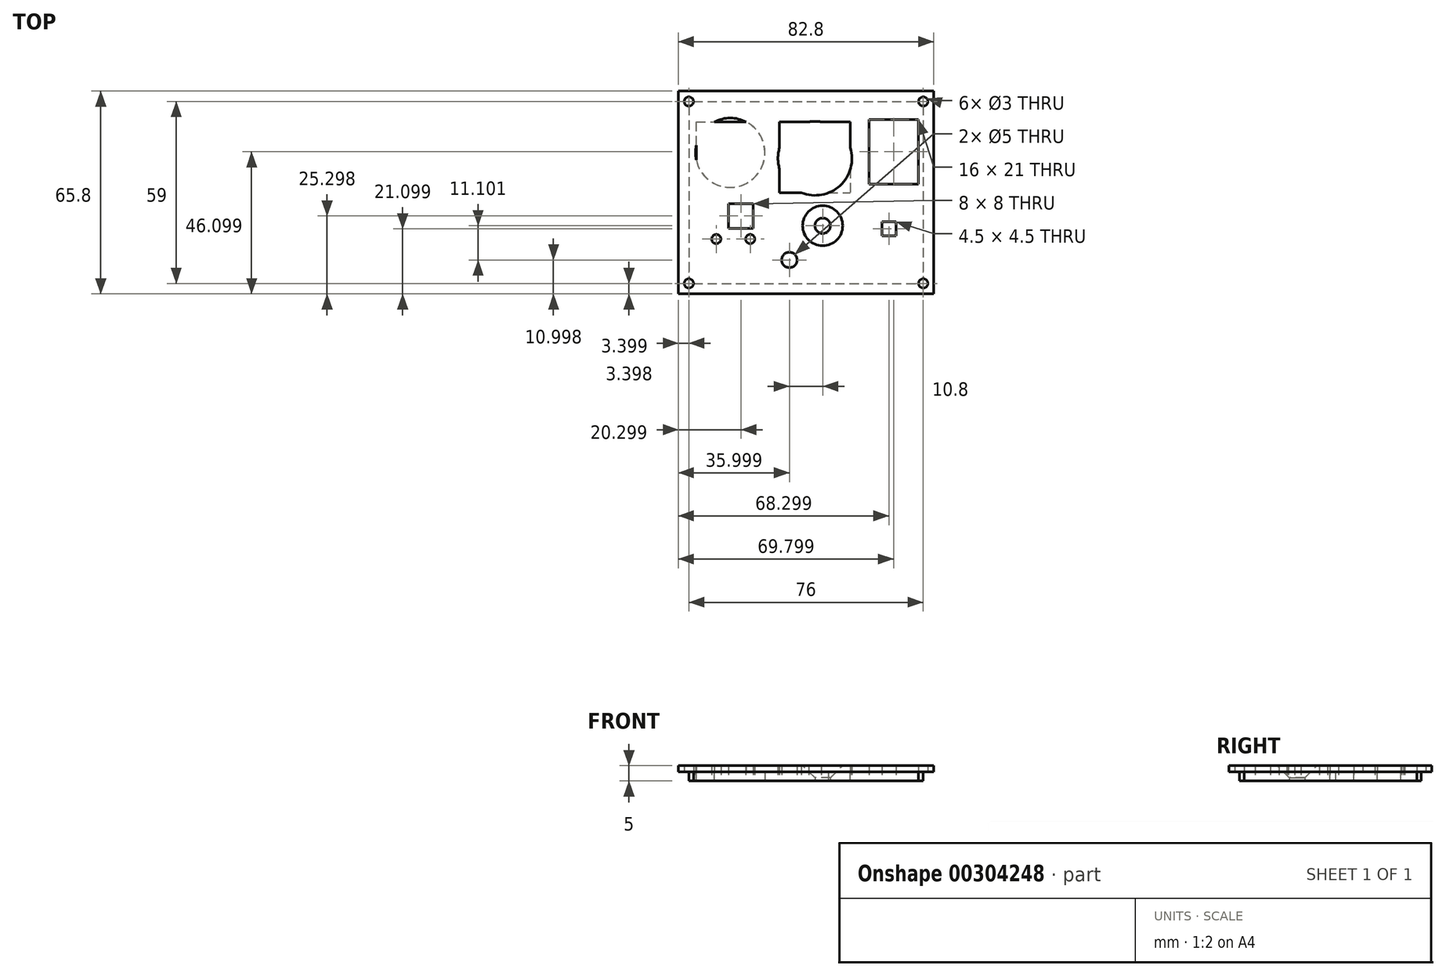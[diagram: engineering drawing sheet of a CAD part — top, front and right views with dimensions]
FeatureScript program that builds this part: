
annotation { "Feature Type Name" : "Feature", "Feature Type Description" : "" }
export const myFeature = defineFeature(function(context is Context, id is Id, definition is map)
    precondition{}
    {
        {
            var Q0;
            Q0=qCreatedBy(makeId("Top.planeOp"),FACE);
            var sketch = newSketch(context, id + "F0", { "sketchPlane" : qUnion([Q0])});
            skLineSegment(sketch, "E0.top", {"start": v(-35.3, 35.45) * mm, "end": v(34.7, 35.45) * mm});
            skLineSegment(sketch, "E0.left", {"start": v(-35.3, -14.55) * mm, "end": v(-35.3, 35.45) * mm});
            skLineSegment(sketch, "E0.right", {"start": v(34.7, -14.25) * mm, "end": v(34.7, 35.45) * mm});
            skCircle(sketch, "E1", {"center": v(-24.3, 25.45) * mm, "radius": 10.25 * mm});
            skCircle(sketch, "E2", {"center": v(3.2, 23.61) * mm, "radius": 12 * mm});
            skLineSegment(sketch, "E3.top", {"start": v(20.7, 15.25) * mm, "end": v(36.7, 15.25) * mm});
            skLineSegment(sketch, "E3.left", {"start": v(20.7, 36.25) * mm, "end": v(20.7, 15.25) * mm});
            skLineSegment(sketch, "E3.right", {"start": v(36.7, 36.25) * mm, "end": v(36.7, 15.25) * mm});
            skCircle(sketch, "E4", {"center": v(5.7, 1.75) * mm, "radius": 2.5 * mm});
            skLineSegment(sketch, "E5.bottom", {"start": v(-24.8, 8.95) * mm, "end": v(-16.8, 8.95) * mm});
            skLineSegment(sketch, "E5.top", {"start": v(-24.8, 0.95) * mm, "end": v(-16.8, 0.95) * mm});
            skLineSegment(sketch, "E5.left", {"start": v(-24.8, 8.95) * mm, "end": v(-24.8, 0.95) * mm});
            skLineSegment(sketch, "E5.right", {"start": v(-16.8, 8.95) * mm, "end": v(-16.8, 0.95) * mm});
            skCircle(sketch, "E6", {"center": v(-28.8, -2.55) * mm, "radius": 1.5 * mm});
            skCircle(sketch, "E7", {"center": v(-17.8, -2.55) * mm, "radius": 1.5 * mm});
            skLineSegment(sketch, "E8.bottom", {"start": v(-41.1, 45.45) * mm, "end": v(41.7, 45.45) * mm});
            skLineSegment(sketch, "E8.top", {"start": v(-41.1, -20.35) * mm, "end": v(41.7, -20.35) * mm});
            skLineSegment(sketch, "E8.left", {"start": v(-41.1, 45.45) * mm, "end": v(-41.1, -20.35) * mm});
            skLineSegment(sketch, "E8.right", {"start": v(41.7, 45.45) * mm, "end": v(41.7, -20.35) * mm});
            skLineSegment(sketch, "E9", {"start": v(-35.3, -14.55) * mm, "end": v(34.7, -14.25) * mm});
            skLineSegment(sketch, "E10.bottom", {"start": v(-8.3, 35.45) * mm, "end": v(14.7, 35.45) * mm});
            skLineSegment(sketch, "E10.top", {"start": v(-8.3, 12.45) * mm, "end": v(14.7, 12.45) * mm});
            skLineSegment(sketch, "E10.left", {"start": v(-8.3, 35.45) * mm, "end": v(-8.3, 12.45) * mm});
            skLineSegment(sketch, "E10.right", {"start": v(14.7, 35.45) * mm, "end": v(14.7, 12.45) * mm});
            skCircle(sketch, "E11.0", {"center": v(-17.8, -2.55) * mm, "radius": 2.5 * mm});
            skCircle(sketch, "E12.0", {"center": v(-28.8, -2.55) * mm, "radius": 2.5 * mm});
            skCircle(sketch, "E13.0", {"center": v(5.7, 1.75) * mm, "radius": 5.5 * mm});
            skCircle(sketch, "E14.0", {"center": v(-24.3, 25.45) * mm, "radius": 11.25 * mm});
            skLineSegment(sketch, "E15.0", {"start": v(-37.7, 42.05) * mm, "end": v(38.3, 42.05) * mm});
            skLineSegment(sketch, "E15.1", {"start": v(-37.7, 42.05) * mm, "end": v(-37.7, -16.95) * mm});
            skLineSegment(sketch, "E15.2", {"start": v(-37.7, -16.95) * mm, "end": v(38.3, -16.95) * mm});
            skLineSegment(sketch, "E15.3", {"start": v(38.3, 42.05) * mm, "end": v(38.3, -16.95) * mm});
            skCircle(sketch, "E16", {"center": v(38.3, 42.05) * mm, "radius": 1.5 * mm});
            skCircle(sketch, "E17", {"center": v(38.3, -16.95) * mm, "radius": 1.5 * mm});
            skCircle(sketch, "E18", {"center": v(-37.7, -16.95) * mm, "radius": 1.5 * mm});
            skCircle(sketch, "E19", {"center": v(-37.7, 42.05) * mm, "radius": 1.5 * mm});
            skLineSegment(sketch, "E20.bottom", {"start": v(29.46, 3) * mm, "end": v(24.96, 3) * mm});
            skLineSegment(sketch, "E20.top", {"start": v(29.46, -1.5) * mm, "end": v(24.96, -1.5) * mm});
            skLineSegment(sketch, "E20.left", {"start": v(29.46, 3) * mm, "end": v(29.46, -1.5) * mm});
            skLineSegment(sketch, "E20.right", {"start": v(24.96, 3) * mm, "end": v(24.96, -1.5) * mm});
            skPoint(sketch, "E20.middle", {"position": v(27.2, 0.75) * mm});
            skLineSegment(sketch, "E21.0", {"start": v(30.46, 4) * mm, "end": v(23.96, 4) * mm});
            skLineSegment(sketch, "E21.1", {"start": v(30.46, 4) * mm, "end": v(30.46, -2.5) * mm});
            skLineSegment(sketch, "E21.2", {"start": v(30.46, -2.5) * mm, "end": v(23.96, -2.5) * mm});
            skLineSegment(sketch, "E21.3", {"start": v(23.96, 4) * mm, "end": v(23.96, -2.5) * mm});
            skLineSegment(sketch, "E22.top", {"start": v(36.7, 36.25) * mm, "end": v(20.7, 36.25) * mm});
            skCircle(sketch, "E23", {"center": v(-5.1, -9.35) * mm, "radius": 2.5 * mm});
            skSolve(sketch);
        }
        {
            var Q0;
            Q0=makeQuery(id+"F0.imprint","IMPRINT",FACE,{"disambiguationData":[TD([[makeQuery(id+"F0.imprint","IMPRINT",EDGE,{"derivedFrom":sQuery(id+"F0.wireOp",EDGE,"E5.bottom")}),1.0]])]});
            var Q1;
            Q1=makeQuery(id+"F0.imprint","IMPRINT",FACE,{"disambiguationData":[TD([[makeQuery(id+"F0.imprint","IMPRINT",EDGE,{"derivedFrom":sQuery(id+"F0.wireOp",EDGE,"dVt12TAh-KZX3-IpFb-r6c2-O29wN0QmCanL")}),-1.0]])]});
            var Q2;
            Q2=makeQuery(id+"F0.imprint","IMPRINT",FACE,{"disambiguationData":[TD([[makeQuery(id+"F0.imprint","IMPRINT",EDGE,{"derivedFrom":sQuery(id+"F0.wireOp",EDGE,"E7")}),-1.0]])]});
            var Q3;
            Q3=makeQuery(id+"F0.imprint","IMPRINT",FACE,{"disambiguationData":[TD([[makeQuery(id+"F0.imprint","IMPRINT",EDGE,{"derivedFrom":sQuery(id+"F0.wireOp",EDGE,"E6")}),-1.0]])]});
            var Q4;
            Q4=makeQuery(id+"F0.imprint","IMPRINT",FACE,{"disambiguationData":[TD([[makeQuery(id+"F0.imprint","IMPRINT",EDGE,{"derivedFrom":sQuery(id+"F0.wireOp",EDGE,"E4")}),-1.0]])]});
            var Q5;
            Q5=makeQuery(id+"F0.imprint","IMPRINT",FACE,{"disambiguationData":[TD([[makeQuery(id+"F0.imprint","IMPRINT",EDGE,{"derivedFrom":sQuery(id+"F0.wireOp",EDGE,"ZIHxxPCL-HTH9-b3vy-h9K7-gBhtkmtwm23M")}),-1.0]])]});
            var Q6;
            Q6=makeQuery(id+"F0.imprint","IMPRINT",FACE,{"disambiguationData":[TD([[makeQuery(id+"F0.imprint","IMPRINT",EDGE,{"derivedFrom":sQuery(id+"F0.wireOp",EDGE,"JInnooty-3ndj-ReXf-Pqlt-8WF16EcbAwln")}),-1.0]])]});
            var Q7;
            {var subQ17=sQuery(id+"F0.wireOp",EDGE,"E3.bottom");Q7=makeQuery(id+"F0.imprint","IMPRINT",FACE,{"disambiguationData":[TD([[makeQuery(id+"F0.imprint","IMPRINT",EDGE,{"derivedFrom":subQ17}),1.0]])]});}
            var Q8;
            {var subQ0=sQuery(id+"F0.wireOp",EDGE,"E10.left");var subQ1=sQuery(id+"F0.wireOp",EDGE,"E2");var subQ2=makeQuery(id+"F0.imprint","INTERSECT",VERTEX,{"disambiguationData":[OD(1.0)],"derivedFrom":[subQ1,subQ0]});Q8=makeQuery(id+"F0.imprint","IMPRINT",FACE,{"disambiguationData":[TD([[makeQuery(id+"F0.imprint","IMPRINT",EDGE,{"disambiguationData":[TD([[subQ2,-1.0]])],"derivedFrom":subQ1}),-1.0]])]});}
            var Q9;
            {var subQ0=sQuery(id+"F0.wireOp",EDGE,"E10.top");var subQ1=sQuery(id+"F0.wireOp",EDGE,"E2");var subQ2=makeQuery(id+"F0.imprint","INTERSECT",VERTEX,{"disambiguationData":[OD(1.0)],"derivedFrom":[subQ1,subQ0]});Q9=makeQuery(id+"F0.imprint","IMPRINT",FACE,{"disambiguationData":[TD([[makeQuery(id+"F0.imprint","IMPRINT",EDGE,{"disambiguationData":[TD([[subQ2,-1.0]])],"derivedFrom":subQ1}),-1.0]])]});}
            var Q10;
            {var subQ0=sQuery(id+"F0.wireOp",EDGE,"E10.bottom");var subQ1=sQuery(id+"F0.wireOp",EDGE,"E2");var subQ2=makeQuery(id+"F0.imprint","INTERSECT",VERTEX,{"disambiguationData":[OD(1.0)],"derivedFrom":[subQ1,subQ0]});Q10=makeQuery(id+"F0.imprint","IMPRINT",FACE,{"disambiguationData":[TD([[makeQuery(id+"F0.imprint","IMPRINT",EDGE,{"disambiguationData":[TD([[subQ2,-1.0]])],"derivedFrom":subQ1}),-1.0]])]});}
            var Q11;
            {var subQ0=sQuery(id+"F0.wireOp",EDGE,"E10.bottom");var subQ1=sQuery(id+"F0.wireOp",EDGE,"E2");var subQ2=makeQuery(id+"F0.imprint","INTERSECT",VERTEX,{"disambiguationData":[OD(0.0)],"derivedFrom":[subQ1,subQ0]});Q11=makeQuery(id+"F0.imprint","IMPRINT",FACE,{"disambiguationData":[TD([[makeQuery(id+"F0.imprint","IMPRINT",EDGE,{"disambiguationData":[TD([[subQ2,1.0]])],"derivedFrom":subQ1}),-1.0]])]});}
            var Q12;
            {var subQ1=sQuery(id+"F0.wireOp",EDGE,"E1");var subQ5=sQuery(id+"F0.wireOp",EDGE,"E0.top");var subQ6=makeQuery(id+"F0.imprint","INTERSECT",VERTEX,{"disambiguationData":[OD(1.0)],"derivedFrom":[subQ5,subQ1]});Q12=makeQuery(id+"F0.imprint","IMPRINT",FACE,{"disambiguationData":[TD([[makeQuery(id+"F0.imprint","IMPRINT",EDGE,{"disambiguationData":[TD([[subQ6,-1.0]])],"derivedFrom":subQ5}),-1.0]])]});}
            var Q13;
            {var subQ0=sQuery(id+"F0.wireOp",EDGE,"E14.0");var subQ1=sQuery(id+"F0.wireOp",EDGE,"E0.top");var subQ2=makeQuery(id+"F0.imprint","INTERSECT",VERTEX,{"disambiguationData":[OD(0.0)],"derivedFrom":[subQ1,subQ0]});Q13=makeQuery(id+"F0.imprint","IMPRINT",FACE,{"disambiguationData":[TD([[makeQuery(id+"F0.imprint","IMPRINT",EDGE,{"disambiguationData":[TD([[subQ2,-1.0]])],"derivedFrom":subQ1}),1.0]])]});}
            var Q14;
            {var subQ0=sQuery(id+"F0.wireOp",EDGE,"E14.0");var subQ1=sQuery(id+"F0.wireOp",EDGE,"E0.top");var subQ2=makeQuery(id+"F0.imprint","INTERSECT",VERTEX,{"disambiguationData":[OD(0.0)],"derivedFrom":[subQ1,subQ0]});Q14=makeQuery(id+"F0.imprint","IMPRINT",FACE,{"disambiguationData":[TD([[makeQuery(id+"F0.imprint","IMPRINT",EDGE,{"disambiguationData":[TD([[subQ2,-1.0]])],"derivedFrom":subQ1}),-1.0]])]});}
            var Q15;
            {var subQ0=sQuery(id+"F0.wireOp",EDGE,"E14.0");var subQ1=sQuery(id+"F0.wireOp",EDGE,"ZaH0KLtd-WIEc-sx8W-STo8-50ybZZVG4Pet");var subQ2=makeQuery(id+"F0.imprint","INTERSECT",VERTEX,{"disambiguationData":[OD(0.0)],"derivedFrom":[subQ1,subQ0]});Q15=makeQuery(id+"F0.imprint","IMPRINT",FACE,{"disambiguationData":[TD([[makeQuery(id+"F0.imprint","IMPRINT",EDGE,{"disambiguationData":[TD([[subQ2,-1.0]])],"derivedFrom":subQ1}),-1.0]])]});}
            var Q16;
            {var subQ0=sQuery(id+"F0.wireOp",EDGE,"E0.left");var subQ1=sQuery(id+"F0.wireOp",EDGE,"E0.top");var subQ2=makeQuery(id+"F0.imprint","INTERSECT",VERTEX,{"derivedFrom":[subQ1,subQ0]});Q16=makeQuery(id+"F0.imprint","IMPRINT",FACE,{"disambiguationData":[TD([[makeQuery(id+"F0.imprint","IMPRINT",EDGE,{"disambiguationData":[TD([[subQ2,-1.0]])],"derivedFrom":subQ1}),-1.0]])]});}
            var Q17;
            {var subQ0=sQuery(id+"F0.wireOp",EDGE,"6fa23354-8f6d-46e2-804e-7588aa67e6be");var subQ1=sQuery(id+"F0.wireOp",EDGE,"E0.top");var subQ2=makeQuery(id+"F0.imprint","INTERSECT",VERTEX,{"derivedFrom":[subQ1,subQ0]});Q17=makeQuery(id+"F0.imprint","IMPRINT",FACE,{"disambiguationData":[TD([[makeQuery(id+"F0.imprint","IMPRINT",EDGE,{"disambiguationData":[TD([[subQ2,-1.0]])],"derivedFrom":subQ1}),-1.0]])]});}
            var Q18;
            {var subQ0=sQuery(id+"F0.wireOp",EDGE,"6fa23354-8f6d-46e2-804e-7588aa67e6be");var subQ1=sQuery(id+"F0.wireOp",EDGE,"E1");var subQ2=makeQuery(id+"F0.imprint","INTERSECT",VERTEX,{"disambiguationData":[OD(0.0)],"derivedFrom":[subQ1,subQ0]});Q18=makeQuery(id+"F0.imprint","IMPRINT",FACE,{"disambiguationData":[TD([[makeQuery(id+"F0.imprint","IMPRINT",EDGE,{"disambiguationData":[TD([[subQ2,-1.0]])],"derivedFrom":subQ1}),-1.0]])]});}
            var Q19;
            Q19=makeQuery(id+"F0.imprint","IMPRINT",FACE,{"disambiguationData":[TD([[makeQuery(id+"F0.imprint","IMPRINT",EDGE,{"derivedFrom":sQuery(id+"F0.wireOp",EDGE,"E8.bottom")}),-1.0]])]});
            var Q20;
            {var subQ0=sQuery(id+"F0.wireOp",EDGE,"E14.0");var subQ1=sQuery(id+"F0.wireOp",EDGE,"E0.left");var subQ2=makeQuery(id+"F0.imprint","INTERSECT",VERTEX,{"disambiguationData":[OD(0.0)],"derivedFrom":[subQ1,subQ0]});Q20=makeQuery(id+"F0.imprint","IMPRINT",FACE,{"disambiguationData":[TD([[makeQuery(id+"F0.imprint","IMPRINT",EDGE,{"disambiguationData":[TD([[subQ2,-1.0]])],"derivedFrom":subQ1}),1.0]])]});}
            var Q21;
            Q21=makeQuery(id+"F0.imprint","IMPRINT",FACE,{"disambiguationData":[TD([[makeQuery(id+"F0.imprint","IMPRINT",EDGE,{"derivedFrom":sQuery(id+"F0.wireOp",EDGE,"E20.bottom")}),-1.0]])]});
            var Q22;
            Q22=makeQuery(id+"F0.imprint","IMPRINT",FACE,{"disambiguationData":[TD([[makeQuery(id+"F0.imprint","IMPRINT",EDGE,{"derivedFrom":sQuery(id+"F0.wireOp",EDGE,"E22.bottom")}),1.0]])]});
            var Q23;
            {var subQ37=sQuery(id+"F0.wireOp",EDGE,"E3.right");Q23=makeQuery(id+"F0.imprint","IMPRINT",FACE,{"disambiguationData":[TD([[makeQuery(id+"F0.imprint","IMPRINT",EDGE,{"derivedFrom":subQ37}),1.0]])]});}
            extrude(context, id + "F1", {"entities" : qUnion([Q0, Q1, Q2, Q3, Q4, Q5, Q6, Q7, Q8, Q9, Q10, Q11, Q12, Q13, Q14, Q15, Q16, Q17, Q18, Q19, Q20, Q21, Q22, Q23]), "depth" : 2 * mm});
        }
        {
            var Q0;
            Q0=makeQuery(id+"F0.imprint","IMPRINT",FACE,{"disambiguationData":[TD([[makeQuery(id+"F0.imprint","IMPRINT",EDGE,{"derivedFrom":sQuery(id+"F0.wireOp",EDGE,"E20.bottom")}),-1.0]])]});
            var Q1;
            {var subQ1=sQuery(id+"F0.wireOp",EDGE,"E0.top");var subQ4=sQuery(id+"F0.wireOp",EDGE,"E14.0");var subQ6=makeQuery(id+"F0.imprint","INTERSECT",VERTEX,{"disambiguationData":[OD(0.0)],"derivedFrom":[subQ1,subQ4]});Q1=makeQuery(id+"F0.imprint","IMPRINT",FACE,{"disambiguationData":[TD([[makeQuery(id+"F0.imprint","IMPRINT",EDGE,{"disambiguationData":[TD([[subQ6,-1.0]])],"derivedFrom":subQ1}),-1.0]])]});}
            var Q2;
            Q2=makeQuery(id+"F0.imprint","IMPRINT",FACE,{"disambiguationData":[TD([[makeQuery(id+"F0.imprint","IMPRINT",EDGE,{"derivedFrom":sQuery(id+"F0.wireOp",EDGE,"E7")}),-1.0]])]});
            var Q3;
            Q3=makeQuery(id+"F0.imprint","IMPRINT",FACE,{"disambiguationData":[TD([[makeQuery(id+"F0.imprint","IMPRINT",EDGE,{"derivedFrom":sQuery(id+"F0.wireOp",EDGE,"E4")}),-1.0]])]});
            var Q4;
            {var subQ0=sQuery(id+"F0.wireOp",EDGE,"E14.0");var subQ1=sQuery(id+"F0.wireOp",EDGE,"E0.top");var subQ2=makeQuery(id+"F0.imprint","INTERSECT",VERTEX,{"disambiguationData":[OD(0.0)],"derivedFrom":[subQ1,subQ0]});Q4=makeQuery(id+"F0.imprint","IMPRINT",FACE,{"disambiguationData":[TD([[makeQuery(id+"F0.imprint","IMPRINT",EDGE,{"disambiguationData":[TD([[subQ2,-1.0]])],"derivedFrom":subQ1}),1.0]])]});}
            var Q5;
            Q5=makeQuery(id+"F0.imprint","IMPRINT",FACE,{"disambiguationData":[TD([[makeQuery(id+"F0.imprint","IMPRINT",EDGE,{"derivedFrom":sQuery(id+"F0.wireOp",EDGE,"E6")}),-1.0]])]});
            var Q6;
            {var subQ0=sQuery(id+"F0.wireOp",EDGE,"E14.0");var subQ1=sQuery(id+"F0.wireOp",EDGE,"E0.left");var subQ2=makeQuery(id+"F0.imprint","INTERSECT",VERTEX,{"disambiguationData":[OD(0.0)],"derivedFrom":[subQ1,subQ0]});Q6=makeQuery(id+"F0.imprint","IMPRINT",FACE,{"disambiguationData":[TD([[makeQuery(id+"F0.imprint","IMPRINT",EDGE,{"disambiguationData":[TD([[subQ2,-1.0]])],"derivedFrom":subQ1}),1.0]])]});}
            extrude(context, id + "F2", {"entities" : qUnion([Q0, Q1, Q2, Q3, Q4, Q5, Q6]), "operationType" : NewBodyOperationType.ADD, "oppositeDirection" : true, "depth" : 3 * mm});
        }
        {
            var Q0;
            Q0=makeQuery(id+"F1.opExtrude","CAP_EDGE",EDGE,{"disambiguationData":[OSD([sQuery(id+"F0.wireOp",EDGE,"E4")])],"isStart":false});
            chamfer(context, id + "F3", {"entities" : qUnion([Q0]), "width" : 4 * mm, "tangentPropagation" : true});
        }
    });
